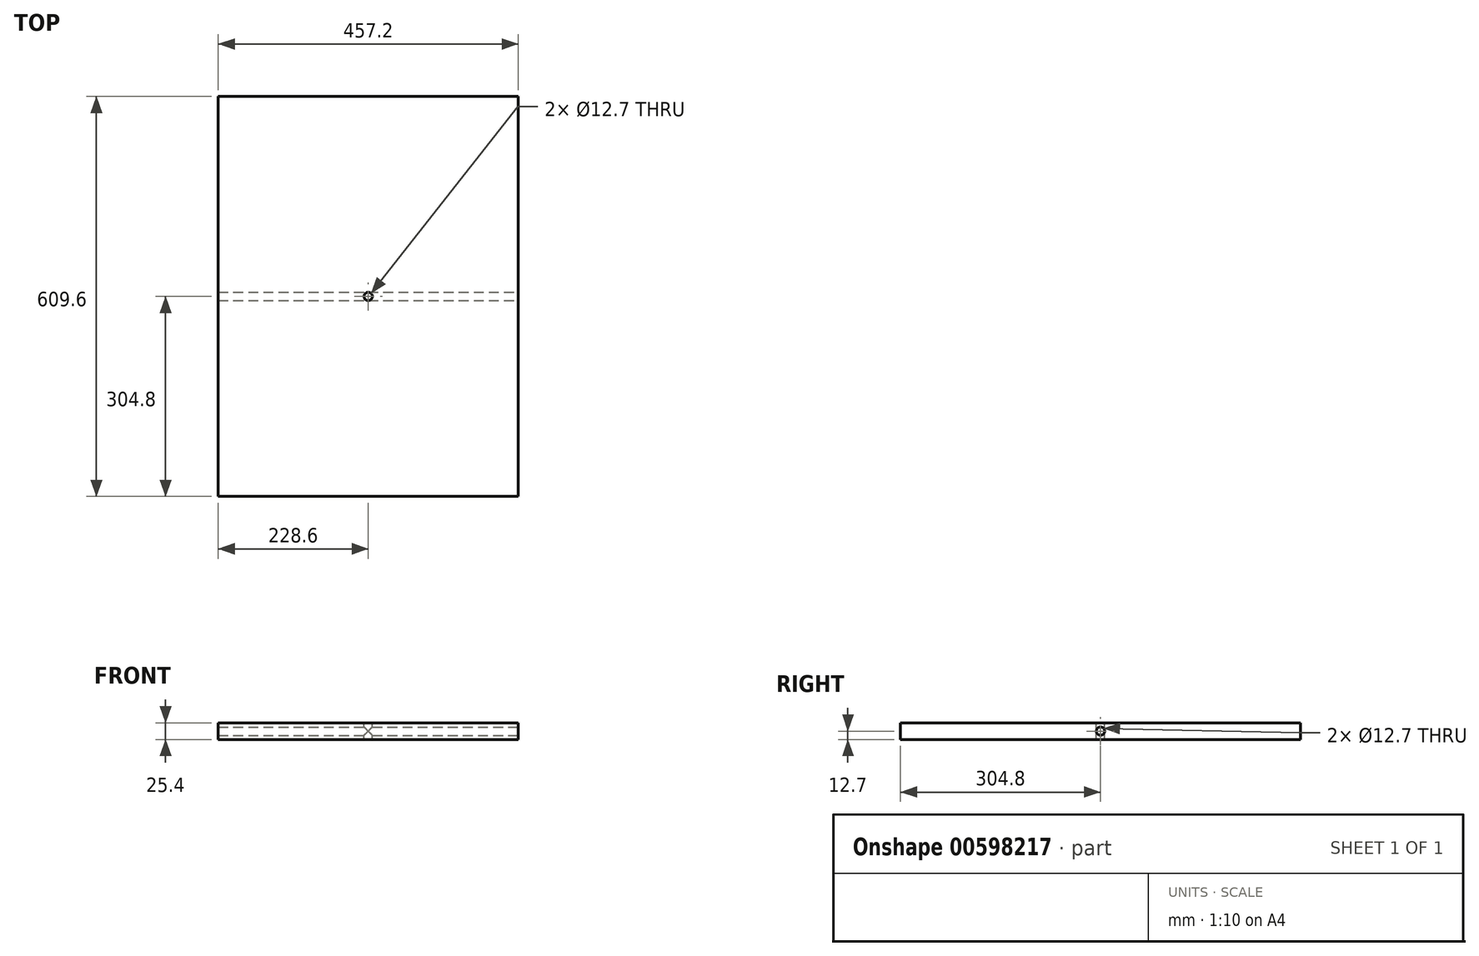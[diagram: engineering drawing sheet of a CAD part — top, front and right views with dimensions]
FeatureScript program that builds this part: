
annotation { "Feature Type Name" : "Feature", "Feature Type Description" : "" }
export const myFeature = defineFeature(function(context is Context, id is Id, definition is map)
    precondition{}
    {
        {
            var Q0;
            Q0=qCreatedBy(makeId("Top.planeOp"),FACE);
            var sketch = newSketch(context, id + "F0", { "sketchPlane" : qUnion([Q0])});
            skLineSegment(sketch, "E0.bottom", {"start": v(228.6, 304.8) * mm, "end": v(-228.6, 304.8) * mm});
            skLineSegment(sketch, "E0.top", {"start": v(228.6, -304.8) * mm, "end": v(-228.6, -304.8) * mm});
            skLineSegment(sketch, "E0.left", {"start": v(228.6, 304.8) * mm, "end": v(228.6, -304.8) * mm});
            skLineSegment(sketch, "E0.right", {"start": v(-228.6, 304.8) * mm, "end": v(-228.6, -304.8) * mm});
            skPoint(sketch, "E0.middle", {"position": v(0, 0) * mm});
            skSolve(sketch);
        }
        {
            var Q0;
            Q0=makeQuery(id+"F0.imprint","IMPRINT",FACE,{"disambiguationData":[TD([[makeQuery(id+"F0.imprint","IMPRINT",EDGE,{"derivedFrom":sQuery(id+"F0.wireOp",EDGE,"E0.bottom")}),1.0]])]});
            extrude(context, id + "F1", {"entities" : qUnion([Q0]), "depth" : 25.4 * mm, "offsetDistance" : 25.4 * mm});
        }
        {
            var Q0;
            Q0=makeQuery(id+"F1.opExtrude","SWEPT_FACE",FACE,{"disambiguationData":[OSD([sQuery(id+"F0.wireOp",EDGE,"E0.left")])]});
            var sketch = newSketch(context, id + "F2", { "sketchPlane" : qUnion([Q0])});
            skCircle(sketch, "E1", {"center": v(0, 12.7) * mm, "radius": 6.35 * mm});
            skSolve(sketch);
        }
        {
            var Q0;
            Q0=makeQuery(id+"F2.imprint","IMPRINT",FACE,{"disambiguationData":[TD([[makeQuery(id+"F2.imprint","IMPRINT",EDGE,{"derivedFrom":sQuery(id+"F2.wireOp",EDGE,"E1")}),1.0]])]});
            extrude(context, id + "F3", {"entities" : qUnion([Q0]), "operationType" : NewBodyOperationType.REMOVE, "oppositeDirection" : true, "depth" : 762 * mm, "offsetDistance" : 25.4 * mm});
        }
        {
            var Q0;
            Q0=makeQuery(id+"F1.opExtrude","CAP_FACE",FACE,{"disambiguationData":[OSD([sQuery(id+"F0.wireOp",EDGE,"E0.bottom"),sQuery(id+"F0.wireOp",EDGE,"E0.top"),sQuery(id+"F0.wireOp",EDGE,"E0.left"),sQuery(id+"F0.wireOp",EDGE,"E0.right")])],"isStart":false});
            var sketch = newSketch(context, id + "F4", { "sketchPlane" : qUnion([Q0])});
            skCircle(sketch, "E2", {"center": v(0, 0) * mm, "radius": 6.35 * mm});
            skSolve(sketch);
        }
        {
            var Q0;
            Q0=makeQuery(id+"F4.imprint","IMPRINT",FACE,{"disambiguationData":[TD([[makeQuery(id+"F4.imprint","IMPRINT",EDGE,{"derivedFrom":sQuery(id+"F4.wireOp",EDGE,"E2")}),1.0]])]});
            extrude(context, id + "F5", {"entities" : qUnion([Q0]), "operationType" : NewBodyOperationType.REMOVE, "oppositeDirection" : true, "depth" : 25.4 * mm, "offsetDistance" : 25.4 * mm});
        }
    });
